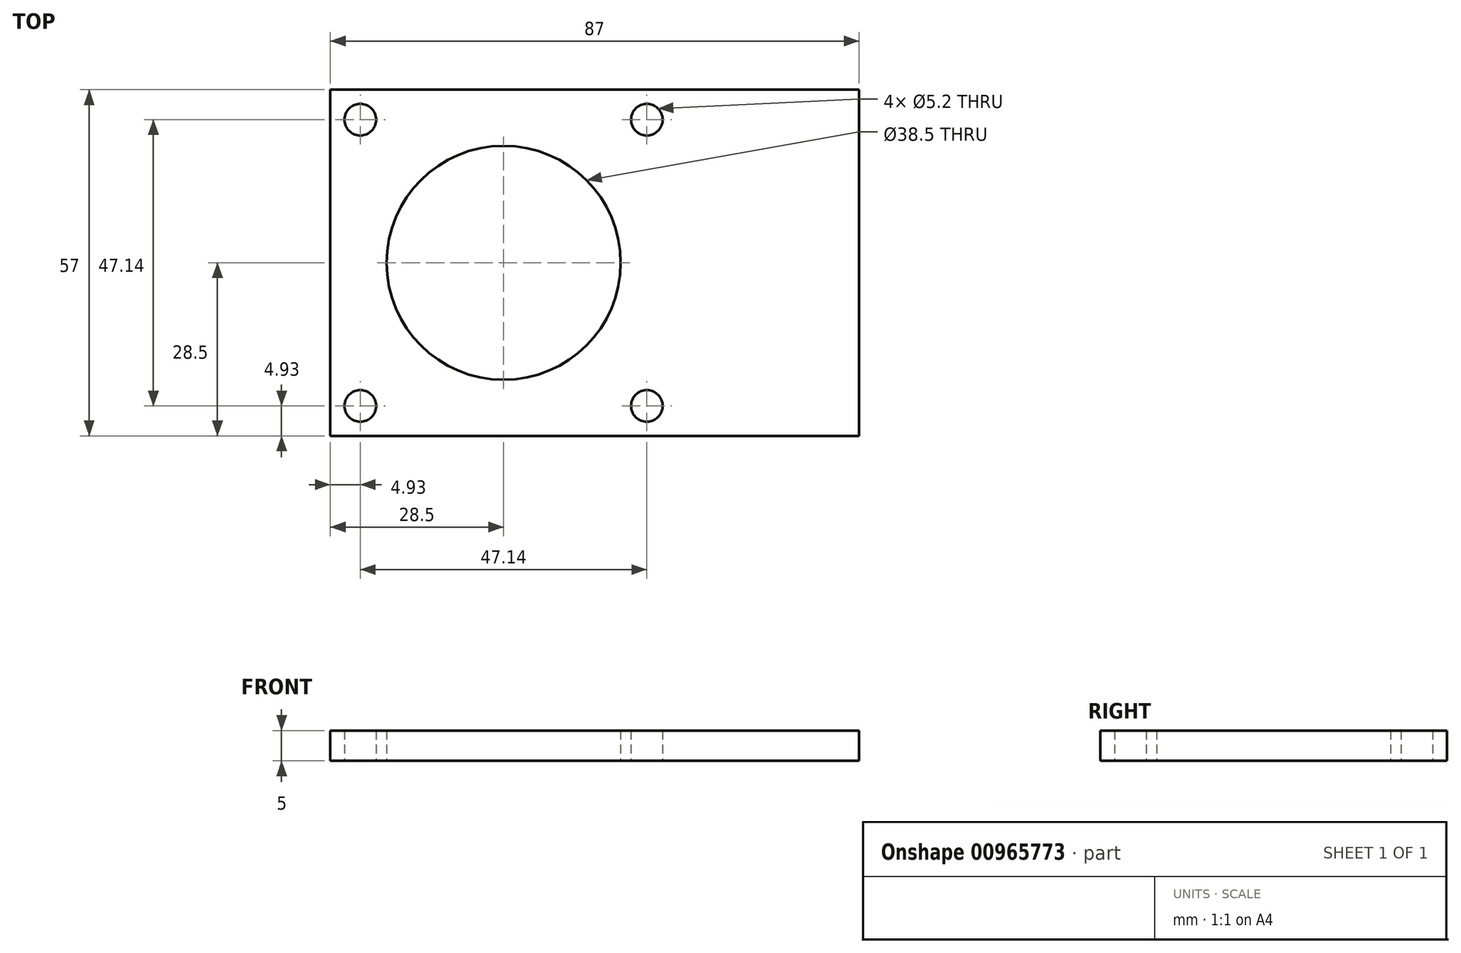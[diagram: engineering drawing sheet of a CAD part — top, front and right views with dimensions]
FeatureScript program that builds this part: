
annotation { "Feature Type Name" : "Feature", "Feature Type Description" : "" }
export const myFeature = defineFeature(function(context is Context, id is Id, definition is map)
    precondition{}
    {
        {
            var Q0;
            Q0=qCreatedBy(makeId("Top.planeOp"),FACE);
            var sketch = newSketch(context, id + "F0", { "sketchPlane" : qUnion([Q0])});
            skLineSegment(sketch, "E0.bottom", {"start": v(28.5, -28.5) * mm, "end": v(-28.5, -28.5) * mm});
            skLineSegment(sketch, "E0.top", {"start": v(28.5, 28.5) * mm, "end": v(-28.5, 28.5) * mm});
            skLineSegment(sketch, "E0.left", {"start": v(28.5, -28.5) * mm, "end": v(28.5, 28.5) * mm, "construction": true});
            skLineSegment(sketch, "E0.right", {"start": v(-28.5, -28.5) * mm, "end": v(-28.5, 28.5) * mm});
            skPoint(sketch, "E0.middle", {"position": v(0, 0) * mm});
            skCircle(sketch, "E1", {"center": v(0, 0) * mm, "radius": 19.25 * mm});
            skLineSegment(sketch, "E2.bottom", {"start": v(23.57, -23.57) * mm, "end": v(-23.57, -23.57) * mm, "construction": true});
            skLineSegment(sketch, "E2.top", {"start": v(23.57, 23.57) * mm, "end": v(-23.57, 23.57) * mm, "construction": true});
            skLineSegment(sketch, "E2.left", {"start": v(23.57, -23.57) * mm, "end": v(23.57, 23.57) * mm, "construction": true});
            skLineSegment(sketch, "E2.right", {"start": v(-23.57, -23.57) * mm, "end": v(-23.57, 23.57) * mm, "construction": true});
            skCircle(sketch, "E3", {"center": v(-23.57, 23.57) * mm, "radius": 2.6 * mm});
            skCircle(sketch, "E4", {"center": v(23.57, 23.57) * mm, "radius": 2.6 * mm});
            skCircle(sketch, "E5", {"center": v(23.57, -23.57) * mm, "radius": 2.6 * mm});
            skCircle(sketch, "E6", {"center": v(-23.57, -23.57) * mm, "radius": 2.6 * mm});
            skLineSegment(sketch, "E7", {"start": v(28.5, -28.5) * mm, "end": v(58.5, -28.5) * mm});
            skLineSegment(sketch, "E8", {"start": v(58.5, -28.5) * mm, "end": v(58.5, 28.5) * mm});
            skLineSegment(sketch, "E9", {"start": v(58.5, 28.5) * mm, "end": v(28.5, 28.5) * mm});
            skSolve(sketch);
        }
        {
            var Q0;
            Q0 = qSketchRegion(id + "F0", true);
            extrude(context, id + "F1", {"entities" : qUnion([Q0]), "depth" : 5 * mm, "offsetDistance" : 25 * mm});
        }
    });
